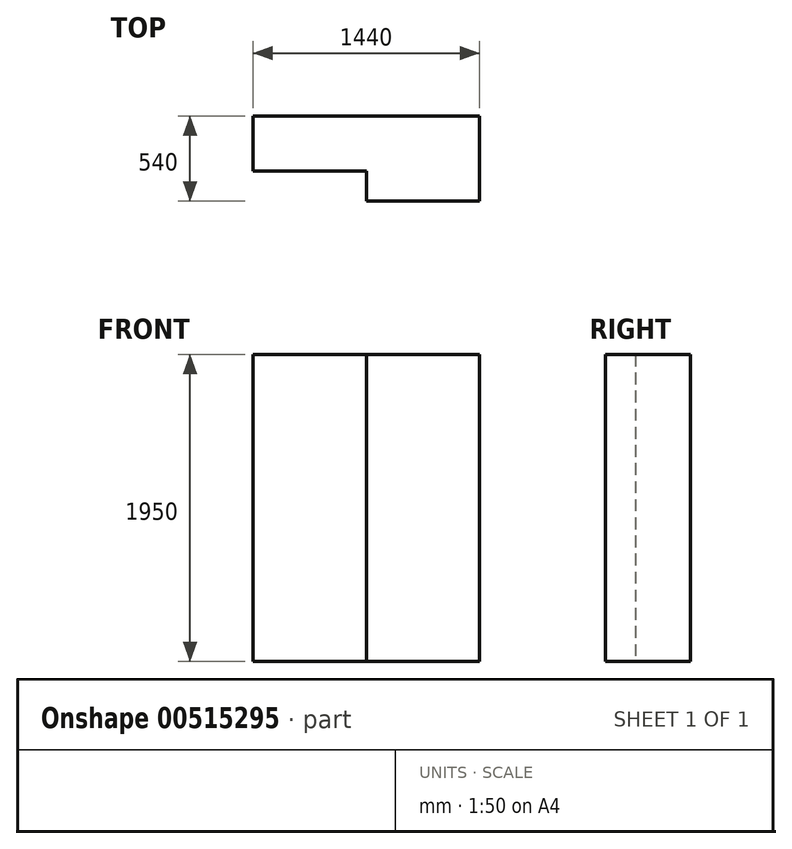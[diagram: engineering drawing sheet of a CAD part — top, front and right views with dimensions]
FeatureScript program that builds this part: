
annotation { "Feature Type Name" : "Feature", "Feature Type Description" : "" }
export const myFeature = defineFeature(function(context is Context, id is Id, definition is map)
    precondition{}
    {
        {
            var Q0;
            Q0=qCreatedBy(makeId("Right.planeOp"),FACE);
            var sketch = newSketch(context, id + "F0", { "sketchPlane" : qUnion([Q0])});
            skLineSegment(sketch, "E0.bottom", {"start": v(270, 975) * mm, "end": v(-270, 975) * mm});
            skLineSegment(sketch, "E0.top", {"start": v(270, -975) * mm, "end": v(-270, -975) * mm});
            skLineSegment(sketch, "E0.left", {"start": v(270, 975) * mm, "end": v(270, -975) * mm});
            skLineSegment(sketch, "E0.right", {"start": v(-270, 975) * mm, "end": v(-270, -975) * mm});
            skPoint(sketch, "E0.middle", {"position": v(0, 0) * mm});
            skSolve(sketch);
        }
        {
            var Q0;
            Q0=qSketchRegion(id+"F0",true);
            extrude(context, id + "F1", {"entities" : qUnion([Q0]), "depth" : 720 * mm, "offsetDistance" : 25 * mm});
        }
        {
            var Q0;
            Q0=makeQuery(id+"F1.opExtrude","CAP_FACE",FACE,{"disambiguationData":[OSD([sQuery(id+"F0.wireOp",EDGE,"E0.bottom"),sQuery(id+"F0.wireOp",EDGE,"E0.top"),sQuery(id+"F0.wireOp",EDGE,"E0.left"),sQuery(id+"F0.wireOp",EDGE,"E0.right")])],"isStart":true});
            var sketch = newSketch(context, id + "F2", { "sketchPlane" : qUnion([Q0])});
            skLineSegment(sketch, "E1.bottom", {"start": v(-270, 975) * mm, "end": v(80, 975) * mm});
            skLineSegment(sketch, "E1.top", {"start": v(-270, -975) * mm, "end": v(80, -975) * mm});
            skLineSegment(sketch, "E1.left", {"start": v(-270, 975) * mm, "end": v(-270, -975) * mm});
            skLineSegment(sketch, "E1.right", {"start": v(80, 975) * mm, "end": v(80, -975) * mm});
            skSolve(sketch);
        }
        {
            var Q0;
            Q0=qSketchRegion(id+"F2",true);
            extrude(context, id + "F3", {"entities" : qUnion([Q0]), "operationType" : NewBodyOperationType.ADD, "depth" : 720 * mm, "offsetDistance" : 25 * mm});
        }
    });
